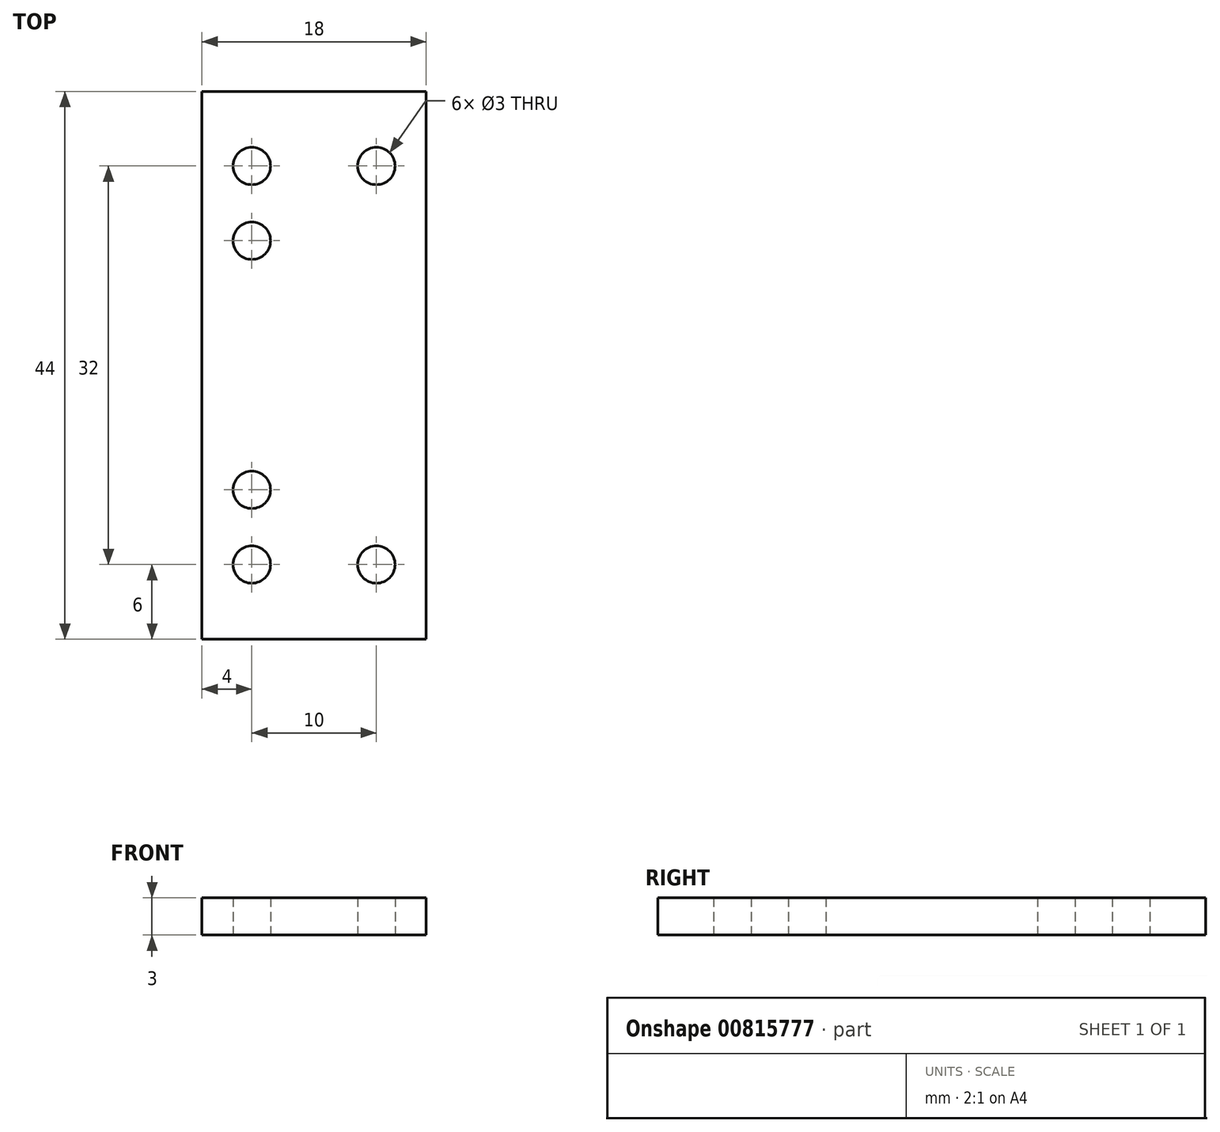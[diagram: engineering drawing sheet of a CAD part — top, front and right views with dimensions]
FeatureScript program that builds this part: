
annotation { "Feature Type Name" : "Feature", "Feature Type Description" : "" }
export const myFeature = defineFeature(function(context is Context, id is Id, definition is map)
    precondition{}
    {
        {
            var Q0;
            Q0=qCreatedBy(makeId("Top.planeOp"),FACE);
            var sketch = newSketch(context, id + "F0", { "sketchPlane" : qUnion([Q0])});
            skLineSegment(sketch, "E0.bottom", {"start": v(9, -22) * mm, "end": v(-9, -22) * mm});
            skLineSegment(sketch, "E0.top", {"start": v(9, 22) * mm, "end": v(-9, 22) * mm});
            skLineSegment(sketch, "E0.left", {"start": v(9, -22) * mm, "end": v(9, 22) * mm});
            skLineSegment(sketch, "E0.right", {"start": v(-9, -22) * mm, "end": v(-9, 22) * mm});
            skPoint(sketch, "E0.middle", {"position": v(0, 0) * mm});
            skLineSegment(sketch, "E1.bottom", {"start": v(5, -16) * mm, "end": v(-5, -16) * mm});
            skLineSegment(sketch, "E1.top", {"start": v(5, 16) * mm, "end": v(-5, 16) * mm});
            skLineSegment(sketch, "E1.left", {"start": v(5, -16) * mm, "end": v(5, 16) * mm});
            skLineSegment(sketch, "E1.right", {"start": v(-5, -16) * mm, "end": v(-5, 16) * mm});
            skLineSegment(sketch, "E2.bottom", {"start": v(-5, 10) * mm, "end": v(-5, 10) * mm});
            skLineSegment(sketch, "E2.top", {"start": v(-5, -10) * mm, "end": v(-5, -10) * mm});
            skLineSegment(sketch, "E2.left", {"start": v(-5, 10) * mm, "end": v(-5, -10) * mm});
            skLineSegment(sketch, "E2.right", {"start": v(-5, 10) * mm, "end": v(-5, -10) * mm});
            skPoint(sketch, "E2.middle", {"position": v(-5, 0) * mm});
            skSolve(sketch);
        }
        {
            var Q0;
            Q0=makeQuery(id+"F0.imprint","IMPRINT",FACE,{"disambiguationData":[TD([[makeQuery(id+"F0.imprint","IMPRINT",EDGE,{"derivedFrom":sQuery(id+"F0.wireOp",EDGE,"E0.bottom")}),-1.0]])]});
            var Q1;
            Q1=makeQuery(id+"F0.imprint","IMPRINT",FACE,{"disambiguationData":[TD([[makeQuery(id+"F0.imprint","IMPRINT",EDGE,{"derivedFrom":sQuery(id+"F0.wireOp",EDGE,"E1.bottom")}),-1.0]])]});
            extrude(context, id + "F1", {"entities" : qUnion([Q0, Q1]), "depth" : 3 * mm, "offsetDistance" : 25 * mm});
        }
        {
            var Q0;
            Q0=sQuery(id+"F0.wireOp",VERTEX,"E1.right.start");
            var Q1;
            Q1=sQuery(id+"F0.wireOp",VERTEX,"E1.top.end");
            var Q2;
            Q2=sQuery(id+"F0.wireOp",VERTEX,"E2.left.start");
            var Q3;
            Q3=sQuery(id+"F0.wireOp",VERTEX,"E2.left.end");
            var Q4;
            Q4=sQuery(id+"F0.wireOp",VERTEX,"E1.bottom.start");
            var Q5;
            Q5=sQuery(id+"F0.wireOp",VERTEX,"E1.top.start");
            var Q6;
            Q6=makeQuery(id+"F1.opExtrude","SWEPT_BODY",BODY,{"disambiguationData":[OSD([sQuery(id+"F0.wireOp",EDGE,"E0.bottom"),sQuery(id+"F0.wireOp",EDGE,"E0.top"),sQuery(id+"F0.wireOp",EDGE,"E0.left"),sQuery(id+"F0.wireOp",EDGE,"E0.right")])]});
            hole(context, id + "F2", {"style" : HoleStyle.SIMPLE, "endStyle" : HoleEndStyle.THROUGH, "oppositeDirection" : true, "holeDiameter" : 3 * mm, "majorDiameter" : 5 * mm, "isTappedThrough" : true, "tappedDepth" : 12 * mm, "tapClearance" : 3, "locations" : qUnion([Q0, Q1, Q2, Q3, Q4, Q5]), "scope" : qUnion([Q6])});
        }
    });
